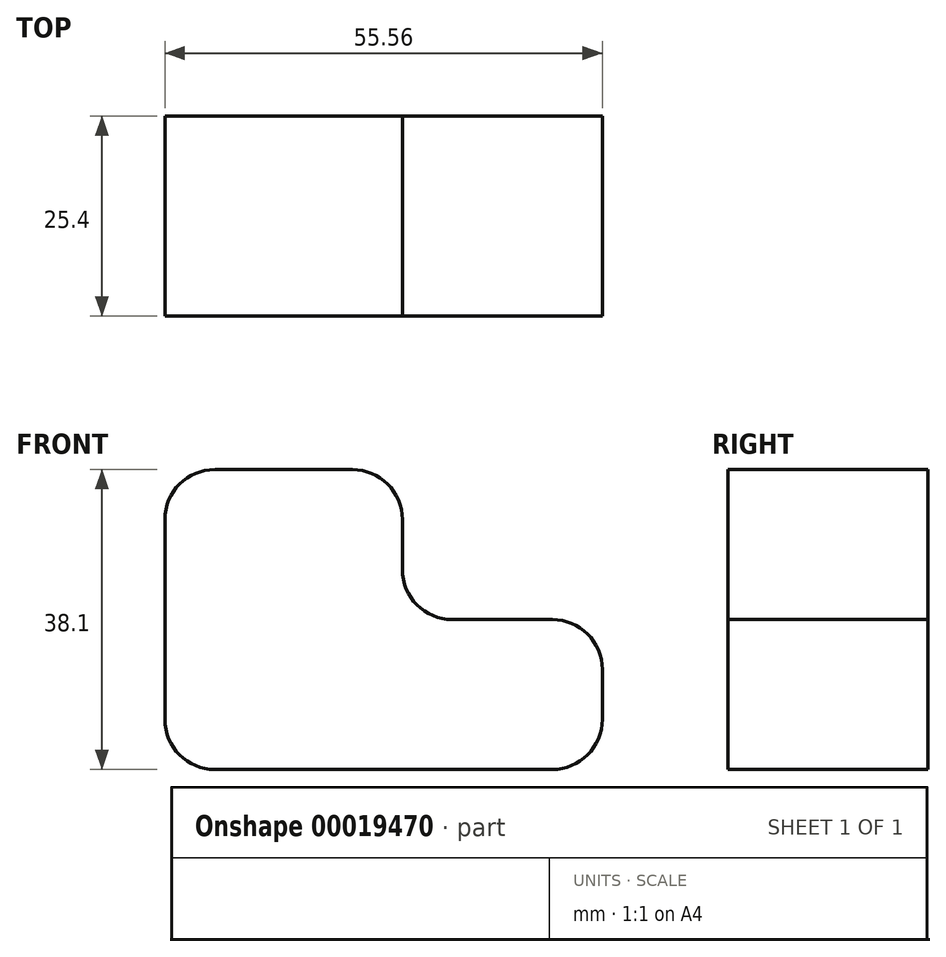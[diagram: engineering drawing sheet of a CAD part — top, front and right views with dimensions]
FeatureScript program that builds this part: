
annotation { "Feature Type Name" : "Feature", "Feature Type Description" : "" }
export const myFeature = defineFeature(function(context is Context, id is Id, definition is map)
    precondition{}
    {
        {
            var Q0;
            Q0=qCreatedBy(makeId("Front.planeOp"),FACE);
            var sketch = newSketch(context, id + "F0", { "sketchPlane" : qUnion([Q0])});
            skLineSegment(sketch, "E0", {"start": v(0, 6.35) * mm, "end": v(0, 31.75) * mm});
            skLineSegment(sketch, "E1", {"start": v(6.35, 0) * mm, "end": v(49.21, 0) * mm});
            skLineSegment(sketch, "E2", {"start": v(6.35, 38.1) * mm, "end": v(23.81, 38.1) * mm});
            skLineSegment(sketch, "E3", {"start": v(30.16, 31.75) * mm, "end": v(30.16, 25.4) * mm});
            skLineSegment(sketch, "E4", {"start": v(36.51, 19.05) * mm, "end": v(49.21, 19.05) * mm});
            skLineSegment(sketch, "E5", {"start": v(55.56, 12.7) * mm, "end": v(55.56, 6.35) * mm});
            skPoint(sketch, "E6.visualSharp", {"position": v(30.16, 38.1) * mm});
            skArc(sketch, "E6.filletArc", {"start": v(30.16, 31.75) * mm, "mid": v(28.3, 36.24) * mm, "end": v(23.81, 38.1) * mm});
            skPoint(sketch, "E7.visualSharp", {"position": v(30.16, 19.05) * mm});
            skArc(sketch, "E7.filletArc", {"start": v(30.16, 25.4) * mm, "mid": v(32.02, 20.9) * mm, "end": v(36.51, 19.05) * mm});
            skPoint(sketch, "E8.visualSharp", {"position": v(55.56, 19.05) * mm});
            skArc(sketch, "E8.filletArc", {"start": v(55.56, 12.7) * mm, "mid": v(53.7, 17.2) * mm, "end": v(49.21, 19.05) * mm});
            skPoint(sketch, "E9.visualSharp", {"position": v(0, 38.1) * mm});
            skArc(sketch, "E9.filletArc", {"start": v(6.35, 38.1) * mm, "mid": v(1.86, 36.24) * mm, "end": v(0, 31.75) * mm});
            skPoint(sketch, "E10.visualSharp", {"position": v(0, 0) * mm});
            skArc(sketch, "E10.filletArc", {"start": v(0, 6.35) * mm, "mid": v(1.86, 1.86) * mm, "end": v(6.35, 0) * mm});
            skPoint(sketch, "E11.visualSharp", {"position": v(55.56, 0) * mm});
            skArc(sketch, "E11.filletArc", {"start": v(49.21, 0) * mm, "mid": v(53.7, 1.86) * mm, "end": v(55.56, 6.35) * mm});
            skSolve(sketch);
        }
        {
            var Q0;
            Q0 = qSketchRegion(id + "F0", true);
            extrude(context, id + "F1", {"entities" : qUnion([Q0]), "depth" : 25.4 * mm});
        }
    });
